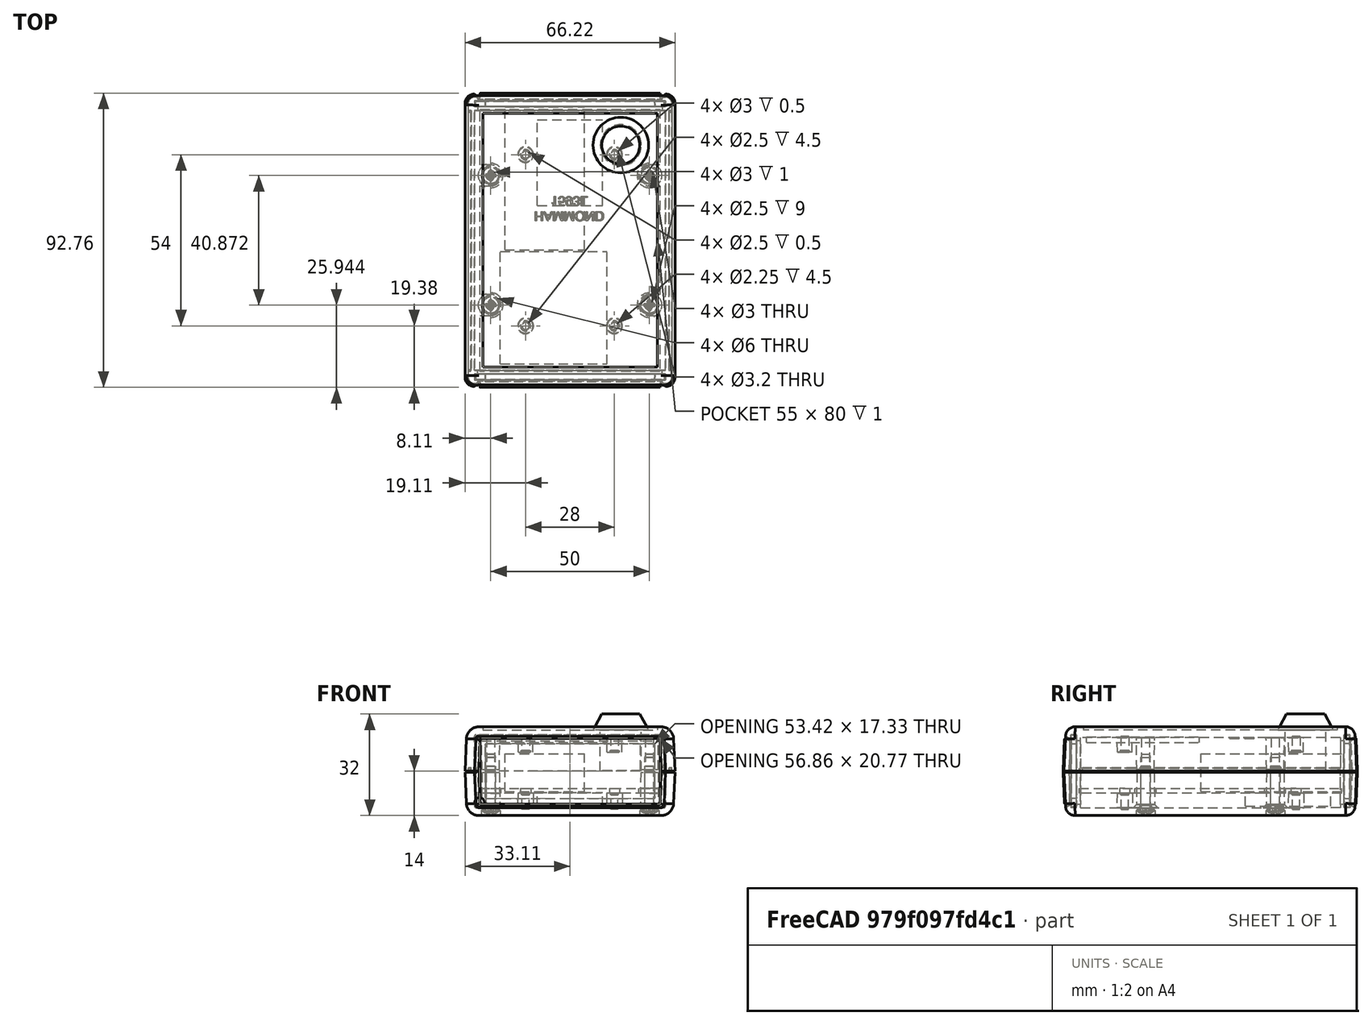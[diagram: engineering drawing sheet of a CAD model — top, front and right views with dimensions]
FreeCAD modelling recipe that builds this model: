
FCSTD DOCUMENT  (FreeCAD 0.16R)
Label: boxl
License: All rights reserved
LicenseURL: http://en.wikipedia.org/wiki/All_rights_reserved
objects: Part::Feature×11, Part::Box×3, App::MeasureDistance×3, Part::Cylinder×1, Part::Cone×1, Part::MultiFuse×1
note: 17 computed .brp shape members not serialized (recipe doc carries the construction recipe); baked Part::Feature solids carry a one-line shape summary decoded from their .brp

FEATURE [Part::Feature] Part__Feature  label="1593L BOTTOM"
  shape: bbox 66.21 x 92.24 x 14.92 mm, 152 faces (baked)
FEATURE [Part::Feature] Part__Feature001  label="1593L Top"
  Placement = pos=(0,0,28) rot=(0,1,0;3.14159rad)
  shape: bbox 66.25 x 92.25 x 229.2 mm, 312 faces (baked)
FEATURE [Part::Feature] Part__Feature002  label="1593K-L-P-Q-X-Y Flat endplate"
  Placement = pos=(0,43.0362,14) rot=(0,0.707107,-0.707107;3.14159rad)
  shape: bbox 60 x 1.7 x 22.7 mm, 10 faces (baked)
FEATURE [Part::Feature] Part__Feature003  label="1593K-L-P-Q-X-Y Flat endplate001"
  Placement = pos=(0,-43.0362,14) rot=(0,0.707107,-0.707107;3.14159rad)
  shape: bbox 60 x 1.7 x 22.7 mm, 10 faces (baked)
FEATURE [Part::Feature] Part__Feature004  label="1593K-L-P-Q-X-Y Contoured Endplate"
  Placement = pos=(0,-43.0362,14) rot=(0,0.707107,-0.707107;3.14159rad)
  shape: bbox 59.51 x 4.203 x 22.63 mm, 31 faces (baked)
FEATURE [Part::Feature] Part__Feature005  label="1593K-L-P-Q-X-Y Contoured Endplate001"
  Placement = pos=(0,43.0362,14) rot=(-1,0,0;1.5708rad)
  shape: bbox 59.51 x 4.203 x 22.63 mm, 31 faces (baked)
FEATURE [Part::Feature] Part__Feature006  label="1593L PCB"
  Placement = pos=(-14,27,7) rot=(1,0,0;3.14159rad)
  shape: bbox 56.61 x 82.66 x 1.6 mm, 26 faces (baked)
FEATURE [Part::Feature] Part__Feature007  label="SC549 (screw #4X 3_4' OH)"
  Placement = pos=(-25,-20.4362,2.53722) rot=(-1,0,0;1.5708rad)
  shape: bbox 5.525 x 5.525 x 18.81 mm, 28 faces (baked)
FEATURE [Part::Feature] Part__Feature008  label="SC549 (screw #4X 3_4' OH)001"
  Placement = pos=(-25,20.4362,2.53722) rot=(-1,0,0;1.5708rad)
  shape: bbox 5.525 x 5.525 x 18.81 mm, 28 faces (baked)
FEATURE [Part::Feature] Part__Feature009  label="SC549 (screw #4X 3_4' OH)002"
  Placement = pos=(25,20.4362,2.53722) rot=(-1,0,0;1.5708rad)
  shape: bbox 5.525 x 5.525 x 18.81 mm, 28 faces (baked)
FEATURE [Part::Feature] Part__Feature010  label="SC549 (screw #4X 3_4' OH)003"
  Placement = pos=(25,-20.4362,2.53722) rot=(-1,0,0;1.5708rad)
  shape: bbox 5.525 x 5.525 x 18.81 mm, 28 faces (baked)
FEATURE [Part::Box] Box  label="Rangefinder"
  Height = 12
  Length = 25
  Placement = pos=(-20.5,-3,7.5) rot=(0,0,1;0rad)
  Width = 45
FEATURE [Part::Box] Box001  label="Battery"
  Height = 4.3
  Length = 20.5
  Placement = pos=(-10.25,11,3) rot=(0,0,1;0rad)
  Width = 27
FEATURE [Part::Cylinder] Cylinder
  Angle = 360
  Height = 12.9
  Placement = pos=(0,0,-12.9) rot=(0,0,1;0rad)
  Radius = 6.45
FEATURE [Part::Cone] Cone
  Angle = 360
  Height = 5
  Radius1 = 8.75
  Radius2 = 6
FEATURE [Part::MultiFuse] Fusion  label="Button"
  Placement = pos=(16,30,27) rot=(0,0,1;0rad)
  Shapes = -> [Cylinder,Cone]
FEATURE [Part::Box] Box002  label="Cube"
  Height = 1.85
  Length = 33.7
  Placement = pos=(-22,-39,23) rot=(0,0,1;0rad)
  Width = 35.5
FEATURE [App::MeasureDistance] Distance  label="Distance: 27.082 mm"
  Distance = 27.082
  P1 = (-5.58699,-26.7287,27)
  P2 = (7.89066,-41.331,8.6)
FEATURE [App::MeasureDistance] Distance001  label="Distance: 14.6458 mm"
  Distance = 14.6458
  P1 = (3.61988,-39,23)
  P2 = (4.92564,-41.331,8.6)
FEATURE [App::MeasureDistance] Distance002  label="Distance: 14.5876 mm"
  Distance = 14.5876
  P1 = (-20.4483,-39,23)
  P2 = (-20.5062,-41.331,8.6)
